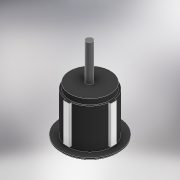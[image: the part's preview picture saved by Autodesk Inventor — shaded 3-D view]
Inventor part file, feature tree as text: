
AUTODESK INVENTOR PART (.ipt)
format: ipt  version: 2021 (Build 250183000, 183)  size: 227,840 bytes
history: native  units: mm
features: sketch x7, extrude x6, fillet x2, revolve x1, pattern_circular x1
ambient origin geometry x8: Origin, YZ Plane, XZ Plane, XY Plane, X Axis, Y Axis, Z Axis, Center Point
bodies: Volumenkörper1 (feature_tree)
feature tree (17):
  extrude  "Extrusion1"  Depth=16.34mm TaperAngle=0.0deg
  extrude  "Extrusion2"  Depth=2.16mm TaperAngle=0.0deg
  extrude  "Extrusion3"  Depth=2.0mm TaperAngle=0.0deg
  extrude  "Extrusion4"  Depth=1.0mm
  fillet  "Rundung1"  Radius=1.0mm
  revolve  "Umdrehung1"
  extrude  "Extrusion5"  Depth=0.25mm
  fillet  "Rundung2"  [1 undecoded]
  pattern_circular  "Runde Anordnung1"  [2 undecoded]
  extrude  "Extrusion6"  Depth=15.0mm TaperAngle=360.0deg
  sketch  "Skizze1"  dims[d0=18.0mm d1=16.34mm d2=0.0mm]
  sketch  "Skizze2"  dims[d3=16.6mm d4=2.16mm d5=0.0mm]
  sketch  "Skizze3"  dims[d6=23.75mm d7=2.0mm d8=0.0mm]
  sketch  "Skizze4"  dims[d9=14.15mm d10=17.0mm d11=1.0mm d12=0.0mm]
  sketch  "Skizze5"  dims[d13=0.25mm d14=0.5mm d15=90.0deg]
  sketch  "Skizze6"  dims[d16=0.75mm]
  sketch  "Skizze7"  dims[d17=15.5mm d18=0.0mm d19=0.1mm d20=40.0mm d21=360.0deg d23=2.75mm d24=15.0mm d25=0.0mm]
note: 3 required parameter values undecoded (feature->parameter linkage not recoverable at this tier; creation-order binding heuristic only, values carry confidence <= 0.55)
